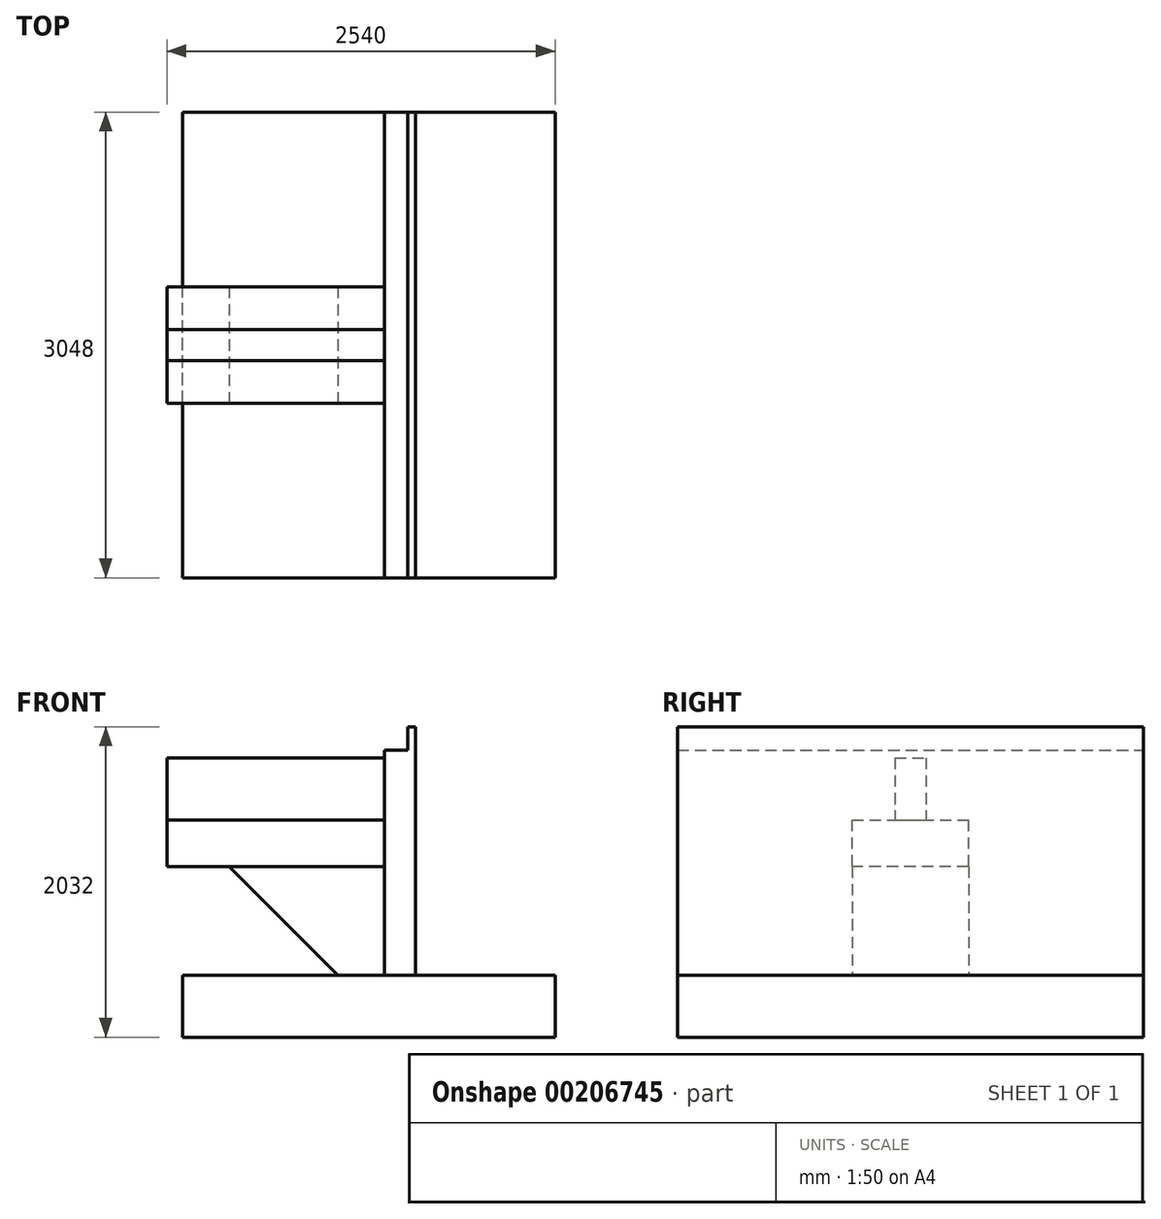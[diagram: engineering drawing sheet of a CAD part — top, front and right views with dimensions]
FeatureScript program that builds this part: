
annotation { "Feature Type Name" : "Feature", "Feature Type Description" : "" }
export const myFeature = defineFeature(function(context is Context, id is Id, definition is map)
    precondition{}
    {
        {
            var Q0;
            Q0=qCreatedBy(makeId("Front.planeOp"),FACE);
            var sketch = newSketch(context, id + "F0", { "sketchPlane" : qUnion([Q0])});
            skLineSegment(sketch, "E0", {"start": v(-1158.55, -609.6) * mm, "end": v(-1158.55, -1016) * mm});
            skLineSegment(sketch, "E1", {"start": v(-1158.55, -1016) * mm, "end": v(1279.85, -1016) * mm});
            skLineSegment(sketch, "E2", {"start": v(1279.85, -1016) * mm, "end": v(1279.85, -609.6) * mm});
            skLineSegment(sketch, "E3", {"start": v(1279.85, -609.6) * mm, "end": v(-1158.55, -609.6) * mm});
            skLineSegment(sketch, "E4", {"start": v(162.25, -609.6) * mm, "end": v(162.25, -203.2) * mm});
            skLineSegment(sketch, "E5", {"start": v(162.25, -203.2) * mm, "end": v(365.45, -203.2) * mm});
            skLineSegment(sketch, "E6", {"start": v(365.45, -203.2) * mm, "end": v(365.45, -609.6) * mm});
            skLineSegment(sketch, "E7", {"start": v(162.25, -203.2) * mm, "end": v(162.25, 0) * mm});
            skLineSegment(sketch, "E8", {"start": v(162.25, 0) * mm, "end": v(365.45, 0) * mm});
            skLineSegment(sketch, "E9", {"start": v(365.45, 0) * mm, "end": v(365.45, -203.2) * mm});
            skLineSegment(sketch, "E10", {"start": v(162.25, 0) * mm, "end": v(162.25, 203.2) * mm});
            skLineSegment(sketch, "E11", {"start": v(162.25, 203.2) * mm, "end": v(365.45, 203.2) * mm});
            skLineSegment(sketch, "E12", {"start": v(365.45, 203.2) * mm, "end": v(365.45, 0) * mm});
            skLineSegment(sketch, "E13", {"start": v(162.25, 203.2) * mm, "end": v(162.25, 406.4) * mm});
            skLineSegment(sketch, "E14", {"start": v(162.25, 406.4) * mm, "end": v(365.45, 406.4) * mm});
            skLineSegment(sketch, "E15", {"start": v(365.45, 406.4) * mm, "end": v(365.45, 203.2) * mm});
            skLineSegment(sketch, "E16", {"start": v(162.25, 406.4) * mm, "end": v(162.25, 609.6) * mm});
            skLineSegment(sketch, "E17", {"start": v(162.25, 609.6) * mm, "end": v(365.45, 609.6) * mm});
            skLineSegment(sketch, "E18", {"start": v(365.45, 609.6) * mm, "end": v(365.45, 406.4) * mm});
            skLineSegment(sketch, "E19", {"start": v(162.25, 609.6) * mm, "end": v(162.25, 812.8) * mm});
            skLineSegment(sketch, "E20", {"start": v(162.25, 812.8) * mm, "end": v(365.45, 812.8) * mm});
            skLineSegment(sketch, "E21", {"start": v(365.45, 812.8) * mm, "end": v(365.45, 609.6) * mm});
            skLineSegment(sketch, "E22", {"start": v(162.25, 812.8) * mm, "end": v(162.25, 863.6) * mm});
            skLineSegment(sketch, "E23", {"start": v(162.25, 863.6) * mm, "end": v(314.65, 863.6) * mm});
            skLineSegment(sketch, "E24", {"start": v(314.65, 863.6) * mm, "end": v(314.65, 1016) * mm});
            skLineSegment(sketch, "E25", {"start": v(314.65, 1016) * mm, "end": v(365.45, 1016) * mm});
            skLineSegment(sketch, "E26", {"start": v(365.45, 1016) * mm, "end": v(365.45, 812.8) * mm});
            skLineSegment(sketch, "E27", {"start": v(162.25, 812.8) * mm, "end": v(-1260.15, 812.8) * mm});
            skLineSegment(sketch, "E28", {"start": v(162.25, 609.6) * mm, "end": v(-1260.15, 609.6) * mm});
            skLineSegment(sketch, "E29", {"start": v(162.25, 406.4) * mm, "end": v(-1260.15, 406.4) * mm});
            skLineSegment(sketch, "E30", {"start": v(162.25, 101.6) * mm, "end": v(-1260.15, 101.6) * mm});
            skLineSegment(sketch, "E31", {"start": v(-40.95, 609.6) * mm, "end": v(-40.95, 406.4) * mm});
            skLineSegment(sketch, "E32", {"start": v(-244.15, 609.6) * mm, "end": v(-244.15, 812.8) * mm});
            skLineSegment(sketch, "E33", {"start": v(-447.35, 609.6) * mm, "end": v(-447.35, 406.4) * mm});
            skLineSegment(sketch, "E34", {"start": v(-853.75, 609.6) * mm, "end": v(-853.75, 406.4) * mm});
            skLineSegment(sketch, "E35", {"start": v(-1260.15, 812.8) * mm, "end": v(-1260.15, 101.6) * mm});
            skLineSegment(sketch, "E36.trimOffspring", {"start": v(-650.55, 609.6) * mm, "end": v(-650.55, 812.8) * mm});
            skLineSegment(sketch, "E37.trimOffspring", {"start": v(-1056.95, 609.6) * mm, "end": v(-1056.95, 812.8) * mm});
            skSolve(sketch);
        }
        {
            var Q0;
            {var subQ1=sQuery(id+"F0.wireOp",EDGE,"E13");Q0=makeQuery(id+"F0.imprint","IMPRINT",FACE,{"disambiguationData":[TD([[makeQuery(id+"F0.imprint","IMPRINT",EDGE,{"derivedFrom":subQ1}),1.0]])]});}
            extrude(context, id + "F1", {"entities" : qUnion([Q0]), "endBound" : BoundingType.SYMMETRIC, "depth" : 762 * mm});
        }
        {
            var Q0;
            {var subQ3=sQuery(id+"F0.wireOp",EDGE,"E37.trimOffspring");Q0=makeQuery(id+"F0.imprint","IMPRINT",FACE,{"disambiguationData":[TD([[makeQuery(id+"F0.imprint","IMPRINT",EDGE,{"derivedFrom":subQ3}),1.0]])]});}
            var Q1;
            {var subQ0=sQuery(id+"F0.wireOp",EDGE,"E16");Q1=makeQuery(id+"F0.imprint","IMPRINT",FACE,{"disambiguationData":[TD([[makeQuery(id+"F0.imprint","IMPRINT",EDGE,{"derivedFrom":subQ0}),1.0]])]});}
            var Q2;
            {var subQ0=sQuery(id+"F0.wireOp",EDGE,"E31");Q2=makeQuery(id+"F0.imprint","IMPRINT",FACE,{"disambiguationData":[TD([[makeQuery(id+"F0.imprint","IMPRINT",EDGE,{"derivedFrom":subQ0}),-1.0]])]});}
            var Q3;
            {var subQ0=sQuery(id+"F0.wireOp",EDGE,"E33");Q3=makeQuery(id+"F0.imprint","IMPRINT",FACE,{"disambiguationData":[TD([[makeQuery(id+"F0.imprint","IMPRINT",EDGE,{"derivedFrom":subQ0}),-1.0]])]});}
            var Q4;
            {var subQ0=sQuery(id+"F0.wireOp",EDGE,"E34");Q4=makeQuery(id+"F0.imprint","IMPRINT",FACE,{"disambiguationData":[TD([[makeQuery(id+"F0.imprint","IMPRINT",EDGE,{"derivedFrom":subQ0}),-1.0]])]});}
            var Q5;
            {var subQ0=sQuery(id+"F0.wireOp",EDGE,"E36.trimOffspring");Q5=makeQuery(id+"F0.imprint","IMPRINT",FACE,{"disambiguationData":[TD([[makeQuery(id+"F0.imprint","IMPRINT",EDGE,{"derivedFrom":subQ0}),1.0]])]});}
            var Q6;
            {var subQ3=sQuery(id+"F0.wireOp",EDGE,"E32");Q6=makeQuery(id+"F0.imprint","IMPRINT",FACE,{"disambiguationData":[TD([[makeQuery(id+"F0.imprint","IMPRINT",EDGE,{"derivedFrom":subQ3}),1.0]])]});}
            var Q7;
            {var subQ1=sQuery(id+"F0.wireOp",EDGE,"E19");Q7=makeQuery(id+"F0.imprint","IMPRINT",FACE,{"disambiguationData":[TD([[makeQuery(id+"F0.imprint","IMPRINT",EDGE,{"derivedFrom":subQ1}),1.0]])]});}
            extrude(context, id + "F2", {"entities" : qUnion([Q0, Q1, Q2, Q3, Q4, Q5, Q6, Q7]), "endBound" : BoundingType.SYMMETRIC, "depth" : 203.2 * mm});
        }
        {
            var Q0;
            Q0=makeQuery(id+"F1.opExtrude","CAP_FACE",FACE,{"disambiguationData":[OSD([sQuery(id+"F0.wireOp",EDGE,"E10"),sQuery(id+"F0.wireOp",EDGE,"E13"),sQuery(id+"F0.wireOp",EDGE,"E29"),sQuery(id+"F0.wireOp",EDGE,"E30"),sQuery(id+"F0.wireOp",EDGE,"E35")])],"isStart":false});
            var sketch = newSketch(context, id + "F3", { "sketchPlane" : qUnion([Q0])});
            skLineSegment(sketch, "E38", {"start": v(162.25, 101.6) * mm, "end": v(162.25, -609.6) * mm});
            skLineSegment(sketch, "E39", {"start": v(162.25, -609.6) * mm, "end": v(-142.55, -609.6) * mm});
            skLineSegment(sketch, "E40", {"start": v(-142.55, -609.6) * mm, "end": v(-853.75, 101.6) * mm});
            skLineSegment(sketch, "E41", {"start": v(-853.75, 101.6) * mm, "end": v(162.25, 101.6) * mm});
            skSolve(sketch);
        }
        {
            var Q0;
            Q0 = qSketchRegion(id + "F3", true);
            extrude(context, id + "F4", {"entities" : qUnion([Q0]), "oppositeDirection" : true, "depth" : 762 * mm});
        }
        {
            var Q0;
            Q0=makeQuery(id+"F0.imprint","IMPRINT",FACE,{"disambiguationData":[TD([[makeQuery(id+"F0.imprint","IMPRINT",EDGE,{"derivedFrom":sQuery(id+"F0.wireOp",EDGE,"E20")}),1.0]])]});
            var Q1;
            Q1=makeQuery(id+"F0.imprint","IMPRINT",FACE,{"disambiguationData":[TD([[makeQuery(id+"F0.imprint","IMPRINT",EDGE,{"derivedFrom":sQuery(id+"F0.wireOp",EDGE,"E17")}),1.0]])]});
            var Q2;
            Q2=makeQuery(id+"F0.imprint","IMPRINT",FACE,{"disambiguationData":[TD([[makeQuery(id+"F0.imprint","IMPRINT",EDGE,{"derivedFrom":sQuery(id+"F0.wireOp",EDGE,"E14")}),1.0]])]});
            var Q3;
            Q3=makeQuery(id+"F0.imprint","IMPRINT",FACE,{"disambiguationData":[TD([[makeQuery(id+"F0.imprint","IMPRINT",EDGE,{"derivedFrom":sQuery(id+"F0.wireOp",EDGE,"E11")}),1.0]])]});
            var Q4;
            {var subQ3=sQuery(id+"F0.wireOp",EDGE,"E8");Q4=makeQuery(id+"F0.imprint","IMPRINT",FACE,{"disambiguationData":[TD([[makeQuery(id+"F0.imprint","IMPRINT",EDGE,{"derivedFrom":subQ3}),1.0]])]});}
            var Q5;
            Q5=makeQuery(id+"F0.imprint","IMPRINT",FACE,{"disambiguationData":[TD([[makeQuery(id+"F0.imprint","IMPRINT",EDGE,{"derivedFrom":sQuery(id+"F0.wireOp",EDGE,"E5")}),1.0]])]});
            var Q6;
            {var subQ0=sQuery(id+"F0.wireOp",EDGE,"E4");Q6=makeQuery(id+"F0.imprint","IMPRINT",FACE,{"disambiguationData":[TD([[makeQuery(id+"F0.imprint","IMPRINT",EDGE,{"derivedFrom":subQ0}),-1.0]])]});}
            extrude(context, id + "F5", {"entities" : qUnion([Q0, Q1, Q2, Q3, Q4, Q5, Q6]), "endBound" : BoundingType.SYMMETRIC, "depth" : 3048 * mm});
        }
        {
            var Q0;
            {var subQ3=sQuery(id+"F0.wireOp",EDGE,"E0");Q0=makeQuery(id+"F0.imprint","IMPRINT",FACE,{"disambiguationData":[TD([[makeQuery(id+"F0.imprint","IMPRINT",EDGE,{"derivedFrom":subQ3}),1.0]])]});}
            extrude(context, id + "F6", {"entities" : qUnion([Q0]), "endBound" : BoundingType.SYMMETRIC, "depth" : 3048 * mm});
        }
    });
